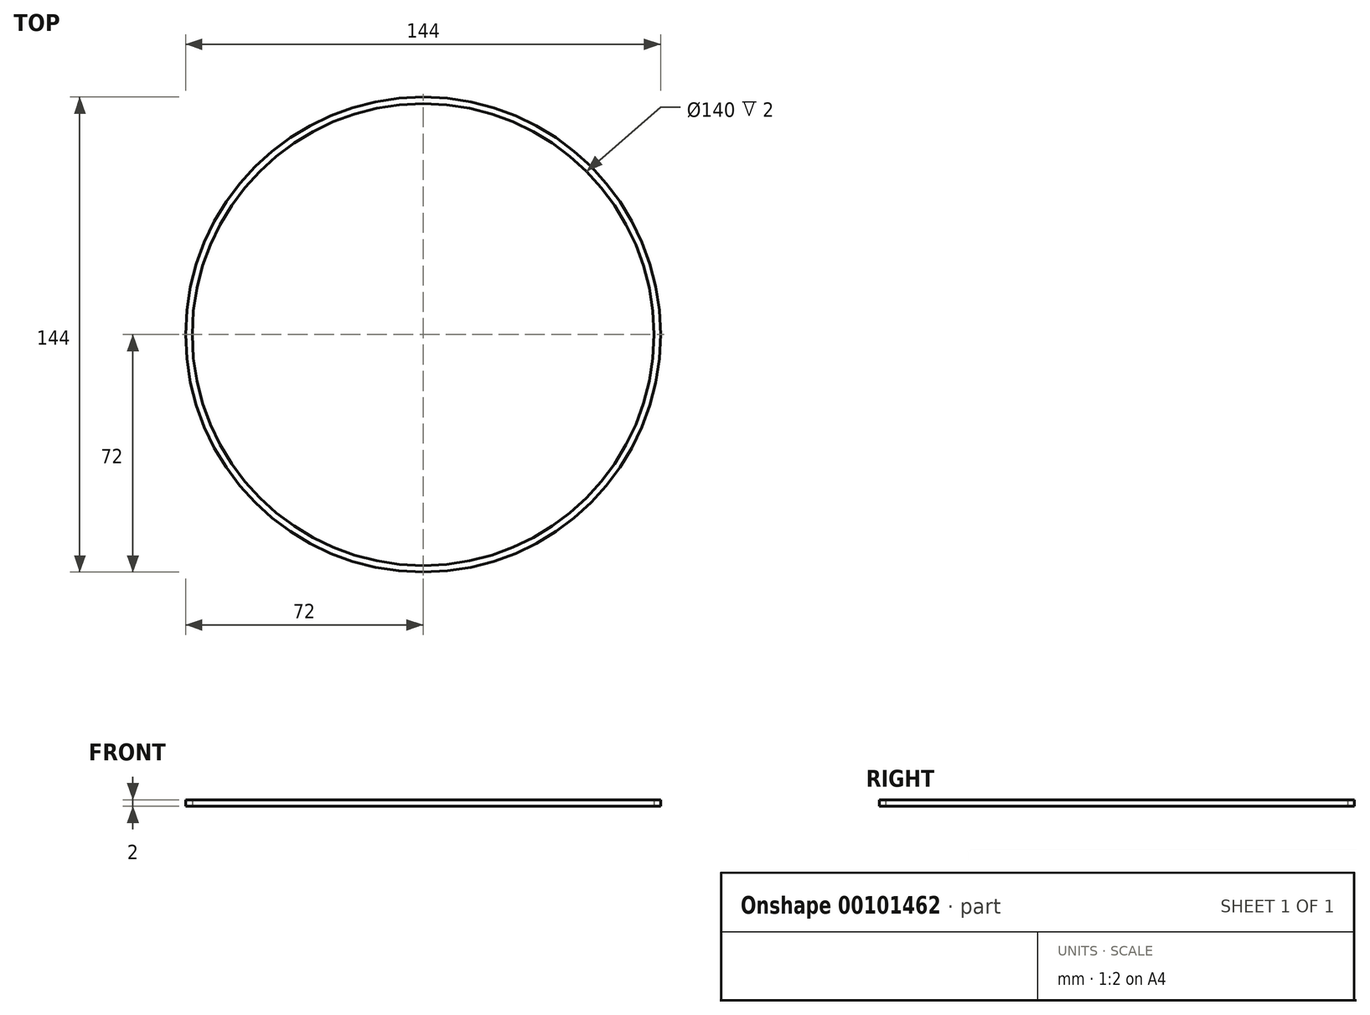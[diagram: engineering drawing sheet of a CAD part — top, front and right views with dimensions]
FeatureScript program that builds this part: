
annotation { "Feature Type Name" : "Feature", "Feature Type Description" : "" }
export const myFeature = defineFeature(function(context is Context, id is Id, definition is map)
    precondition{}
    {
        {
            var Q0;
            Q0=qCreatedBy(makeId("Top.planeOp"),FACE);
            var sketch = newSketch(context, id + "F0", { "sketchPlane" : qUnion([Q0])});
            skCircle(sketch, "E0", {"center": v(0, 0) * mm, "radius": 72 * mm});
            skSolve(sketch);
        }
        {
            var Q0;
            Q0=qCreatedBy(makeId("Front.planeOp"),FACE);
            var sketch = newSketch(context, id + "F1", { "sketchPlane" : qUnion([Q0])});
            skLineSegment(sketch, "E1.bottom", {"start": v(72, 0) * mm, "end": v(70, 0) * mm});
            skLineSegment(sketch, "E1.top", {"start": v(72, 2) * mm, "end": v(70, 2) * mm});
            skLineSegment(sketch, "E1.left", {"start": v(72, 0) * mm, "end": v(72, 2) * mm});
            skLineSegment(sketch, "E1.right", {"start": v(70, 0) * mm, "end": v(70, 2) * mm});
            skSolve(sketch);
        }
        {
            var Q0;
            Q0 = qSketchRegion(id + "F1", true);
            var Q1;
            Q1=sQuery(id+"F0.wireOp",EDGE,"E0");
            revolve(context, id + "F2", {"entities" : qUnion([Q0]), "axis" : qUnion([Q1]), "revolveType" : RevolveType.FULL});
        }
    });
